# Revit family: Projection_Screen-Draper_Inc.-Targa_Large
name_source: partatom
category: Specialty Equipment
units: mm (PartAtom-declared; Revit-internal decimal feet)

## family parameters
Always vertical = Yes
Classification Number = 23.85.10.14.31
Cut with Voids When Loaded = No
Enable Cutting in Views = No
Maintain Annotation Orientation = No
Part Type = Normal
Room Calculation Point = No
Round Connector Dimension = Use Diameter
Shared = No
Work Plane-Based = No

## types (18) — shared parameters
Apparent Load = 132 VA
Case Material = Paint - Draper - White
Default Elevation = 0"
Depth = 6 3/4"
Description = Projection Screen
Frequency = 60 Hz
Manufacturer = Draper Inc.
Model = Targa Large
Number of Poles = 1
Product Documentation Link = http://www.draperinc.com
Product Name = Targa  Large Electric Projection Screen
Product Page URL = http://www.draperinc.com
Projection Screen Material = Fabric - Draper - CH1900E - Pearl White
URL = http://www.DraperInc.com
Width = 4 3/4"

## per-type parameters (varying)
| type | Border | Image Area | Image Height | Image Height Constraint | Image Length | Image Length Constraint | Length | Overall Size | Screen | Screen Drop | Voltage |
| AV Format - 16’  x 16’  - 220 V | No | 192" x 192" | 16' - 0" | 15' - 11 3/4" | 16' - 0" | 15' - 11 3/4" | 16' - 8 7/8" | 192" x 192" | 16' - 0" | 16' - 0" | 220 V |
| AV Format - 12’  x 16’  - 220 V | No | 144" x 192" | 12' - 0" | 11' - 11 3/4" | 16' - 0" | 15' - 11 3/4" | 16' - 8 7/8" | 144" x 192" | 16' - 0" | 12' - 0" | 220 V |
| AV Format - 14’  x 14’  - 220 V | No | 168" x 168" | 14' - 0" | 13' - 11 3/4" | 14' - 0" | 13' - 11 3/4" | 14' - 8 7/8" | 168" x 168" | 14' - 0" | 14' - 0" | 220 V |
| 16:10 Format - 222" - 220 V | Yes | 117 1/2" x 188" | 9' - 9 1/2" | 9' - 9 1/2" | 15' - 8" | 15' - 8" | 16' - 8 7/8" | 122" x 192" | 16' - 0" | 10' - 2" | 220 V |
| 16:10 Format - 198" - 220 V | Yes | 105" x 168" | 8' - 9" | 8' - 9" | 14' - 0" | 14' - 0" | 15' - 0 7/8" | 110" x 172" | 14' - 4" | 9' - 2" | 220 V |
| 16:9 HDTV Format - 220" - 220 V | Yes | 106" x 188" | 8' - 10" | 8' - 10" | 15' - 8" | 15' - 8" | 16' - 8 7/8" | 111" x 192" | 16' - 0" | 9' - 3" | 220 V |
| 16:9 HDTV Format - 193" - 220 V | Yes | 94 1/2" x 168" | 7' - 10 1/2" | 7' - 10 1/2" | 14' - 0" | 14' - 0" | 15' - 0 7/8" | 99 1/2" x 172" | 14' - 4" | 8' - 3 1/2" | 220 V |
| 4:3 NTSC/PAL Video Format - 240" - 220 V | Yes | 141" x 188" | 11' - 9" | 11' - 9" | 15' - 8" | 15' - 8" | 16' - 8 7/8" | 146" x 192" | 16' - 0" | 12' - 2" | 220 V |
| 4:3 NTSC/PAL Video Format - 210" - 220 V | Yes | 126" x 168" | 10' - 6" | 10' - 6" | 14' - 0" | 14' - 0" | 15' - 0 7/8" | 131" x 172" | 14' - 4" | 10' - 11" | 220 V |
| AV Format - 16’  x 16’  - 110 V | No | 192" x 192" | 16' - 0" | 15' - 11 3/4" | 16' - 0" | 15' - 11 3/4" | 16' - 8 7/8" | 192" x 192" | 16' - 0" | 16' - 0" | 110 V |
| AV Format - 12’  x 16’  - 110 V | No | 144" x 192" | 12' - 0" | 11' - 11 3/4" | 16' - 0" | 15' - 11 3/4" | 16' - 8 7/8" | 144" x 192" | 16' - 0" | 12' - 0" | 110 V |
| AV Format - 14’  x 14’  - 110 V | No | 168" x 168" | 14' - 0" | 13' - 11 3/4" | 14' - 0" | 13' - 11 3/4" | 14' - 8 7/8" | 168" x 168" | 14' - 0" | 14' - 0" | 110 V |
| 16:10 Format - 222" - 110 V | Yes | 117 1/2" x 188" | 9' - 9 1/2" | 9' - 9 1/2" | 15' - 8" | 15' - 8" | 16' - 8 7/8" | 122" x 192" | 16' - 0" | 10' - 2" | 110 V |
| 16:10 Format - 198" - 110 V | Yes | 105" x 168" | 8' - 9" | 8' - 9" | 14' - 0" | 14' - 0" | 15' - 0 7/8" | 110" x 172" | 14' - 4" | 9' - 2" | 110 V |
| 16:9 HDTV Format - 220" - 110 V | Yes | 106" x 188" | 8' - 10" | 8' - 10" | 15' - 8" | 15' - 8" | 16' - 8 7/8" | 111" x 192" | 16' - 0" | 9' - 3" | 110 V |
| 16:9 HDTV Format - 193" - 110 V | Yes | 94 1/2" x 168" | 7' - 10 1/2" | 7' - 10 1/2" | 14' - 0" | 14' - 0" | 15' - 0 7/8" | 99 1/2" x 172" | 14' - 4" | 8' - 3 1/2" | 110 V |
| 4:3 NTSC/PAL Video Format - 240" - 110 V | Yes | 141" x 188" | 11' - 9" | 11' - 9" | 15' - 8" | 15' - 8" | 16' - 8 7/8" | 146" x 192" | 16' - 0" | 12' - 2" | 110 V |
| 4:3 NTSC/PAL Video Format - 210" - 110 V | Yes | 126" x 168" | 10' - 6" | 10' - 6" | 14' - 0" | 14' - 0" | 15' - 0 7/8" | 131" x 172" | 14' - 4" | 10' - 11" | 110 V |

## geometry (parser evidence)
native form markers: Sweep x1
no freeform markers — native parametric forms only
